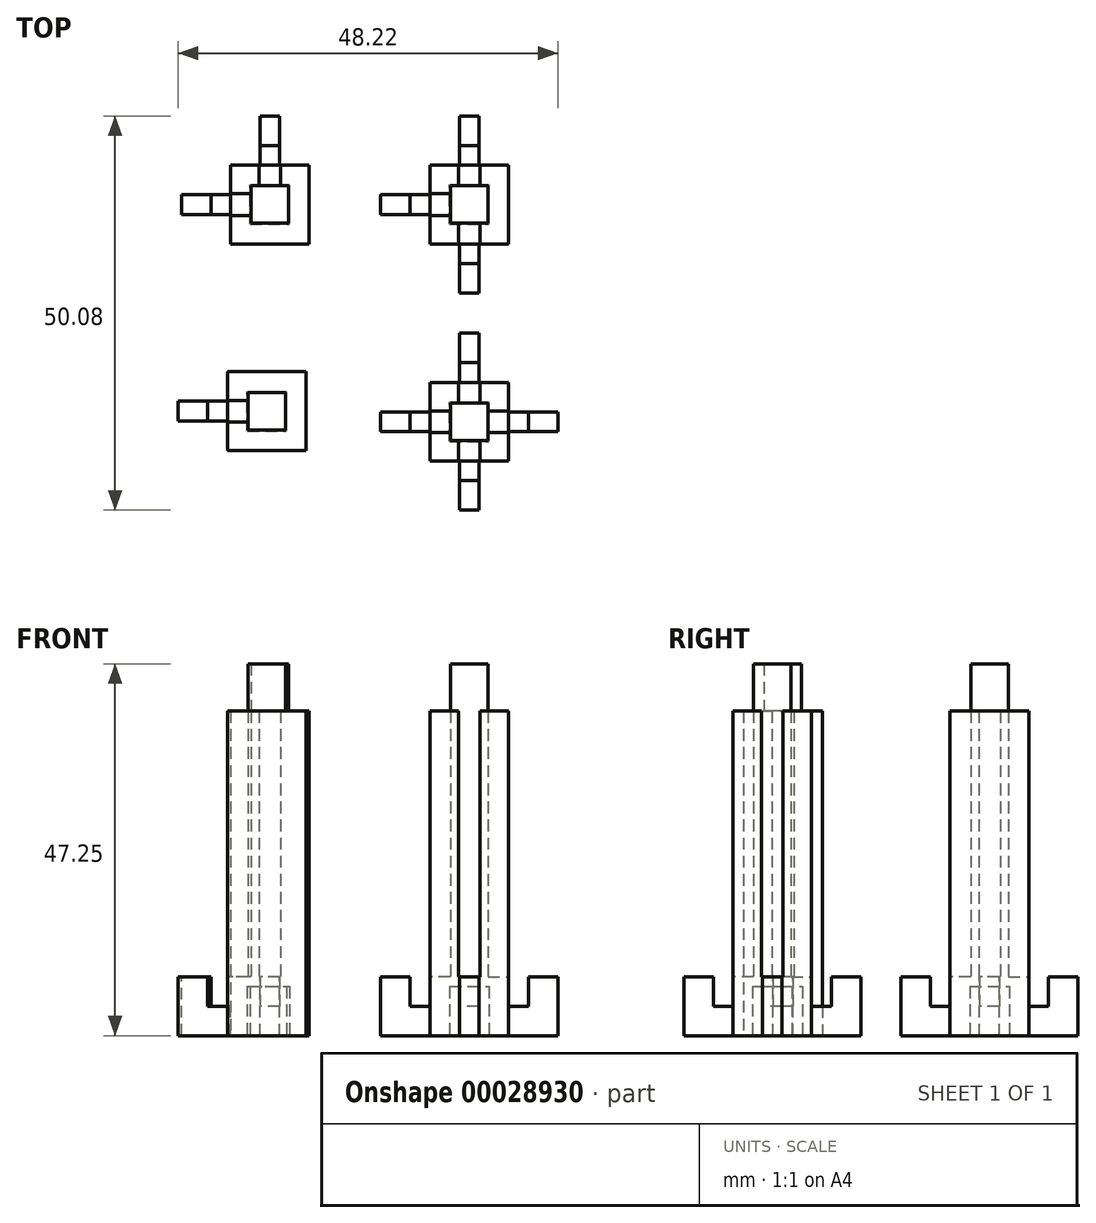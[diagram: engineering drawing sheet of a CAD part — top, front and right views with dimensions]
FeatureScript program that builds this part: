
annotation { "Feature Type Name" : "Feature", "Feature Type Description" : "" }
export const myFeature = defineFeature(function(context is Context, id is Id, definition is map)
    precondition{}
    {
        {
            var Q0;
            Q0=qCreatedBy(makeId("Top.planeOp"),FACE);
            var sketch = newSketch(context, id + "F0", { "sketchPlane" : qUnion([Q0])});
            skLineSegment(sketch, "E0.bottom", {"start": v(0, 0) * mm, "end": v(10, 0) * mm});
            skLineSegment(sketch, "E0.top", {"start": v(0, 10) * mm, "end": v(10, 10) * mm});
            skLineSegment(sketch, "E0.left", {"start": v(0, 0) * mm, "end": v(0, 10) * mm});
            skLineSegment(sketch, "E0.right", {"start": v(10, 0) * mm, "end": v(10, 10) * mm});
            skSolve(sketch);
        }
        {
            var Q0;
            Q0=makeQuery(id+"F0.imprint","IMPRINT",FACE,{"disambiguationData":[TD([[makeQuery(id+"F0.imprint","IMPRINT",EDGE,{"derivedFrom":sQuery(id+"F0.wireOp",EDGE,"E0.bottom")}),1.0]])]});
            extrude(context, id + "F1", {"entities" : qUnion([Q0]), "depth" : 41.25 * mm});
        }
        {
            var Q0;
            Q0=makeQuery(id+"F1.opExtrude","CAP_FACE",FACE,{"disambiguationData":[OSD([sQuery(id+"F0.wireOp",EDGE,"E0.bottom"),sQuery(id+"F0.wireOp",EDGE,"E0.top"),sQuery(id+"F0.wireOp",EDGE,"E0.left"),sQuery(id+"F0.wireOp",EDGE,"E0.right")])],"isStart":false});
            var sketch = newSketch(context, id + "F2", { "sketchPlane" : qUnion([Q0])});
            skLineSegment(sketch, "E1.bottom", {"start": v(2.62, 7.38) * mm, "end": v(7.38, 7.38) * mm});
            skLineSegment(sketch, "E1.top", {"start": v(2.62, 2.62) * mm, "end": v(7.38, 2.62) * mm});
            skLineSegment(sketch, "E1.left", {"start": v(2.62, 7.37) * mm, "end": v(2.62, 2.63) * mm});
            skLineSegment(sketch, "E1.right", {"start": v(7.38, 7.37) * mm, "end": v(7.38, 2.63) * mm});
            skLineSegment(sketch, "E2", {"start": v(5, 10) * mm, "end": v(5, 0) * mm, "construction": true});
            skLineSegment(sketch, "E3", {"start": v(0, 5) * mm, "end": v(10, 5) * mm, "construction": true});
            skSolve(sketch);
        }
        {
            var Q0;
            Q0=makeQuery(id+"F2.imprint","IMPRINT",FACE,{"disambiguationData":[TD([[makeQuery(id+"F2.imprint","IMPRINT",EDGE,{"derivedFrom":sQuery(id+"F2.wireOp",EDGE,"E1.bottom")}),-1.0]])]});
            extrude(context, id + "F3", {"entities" : qUnion([Q0]), "operationType" : NewBodyOperationType.ADD, "depth" : 6 * mm});
        }
        {
            var Q0;
            Q0=makeQuery(id+"F1.opExtrude","CAP_FACE",FACE,{"disambiguationData":[OSD([sQuery(id+"F0.wireOp",EDGE,"E0.bottom"),sQuery(id+"F0.wireOp",EDGE,"E0.top"),sQuery(id+"F0.wireOp",EDGE,"E0.left"),sQuery(id+"F0.wireOp",EDGE,"E0.right")])],"isStart":true});
            var sketch = newSketch(context, id + "F4", { "sketchPlane" : qUnion([Q0])});
            skLineSegment(sketch, "E4.bottom", {"start": v(2.5, -2.5) * mm, "end": v(7.5, -2.5) * mm});
            skLineSegment(sketch, "E4.top", {"start": v(2.5, -7.5) * mm, "end": v(7.5, -7.5) * mm});
            skLineSegment(sketch, "E4.left", {"start": v(2.5, -2.5) * mm, "end": v(2.5, -7.5) * mm});
            skLineSegment(sketch, "E4.right", {"start": v(7.5, -2.5) * mm, "end": v(7.5, -7.5) * mm});
            skLineSegment(sketch, "E5", {"start": v(0, 0) * mm, "end": v(10, -10) * mm, "construction": true});
            skLineSegment(sketch, "E6", {"start": v(10, 0) * mm, "end": v(0, -10) * mm, "construction": true});
            skSolve(sketch);
        }
        {
            var Q0;
            Q0=makeQuery(id+"F4.imprint","IMPRINT",FACE,{"disambiguationData":[TD([[makeQuery(id+"F4.imprint","IMPRINT",EDGE,{"derivedFrom":sQuery(id+"F4.wireOp",EDGE,"E4.bottom")}),-1.0]])]});
            extrude(context, id + "F5", {"entities" : qUnion([Q0]), "operationType" : NewBodyOperationType.REMOVE, "oppositeDirection" : true, "depth" : 6.25 * mm});
        }
        {
            var Q0;
            Q0=makeQuery(id+"F1.opExtrude","SWEPT_FACE",FACE,{"disambiguationData":[OSD([sQuery(id+"F0.wireOp",EDGE,"E0.left")])]});
            var sketch = newSketch(context, id + "F6", { "sketchPlane" : qUnion([Q0])});
            skLineSegment(sketch, "E7.bottom", {"start": v(-6.25, 0) * mm, "end": v(-3.75, 0) * mm});
            skLineSegment(sketch, "E7.top", {"start": v(-6.25, 7.5) * mm, "end": v(-3.75, 7.5) * mm});
            skLineSegment(sketch, "E7.left", {"start": v(-6.25, 0) * mm, "end": v(-6.25, 7.5) * mm});
            skLineSegment(sketch, "E7.right", {"start": v(-3.75, 0) * mm, "end": v(-3.75, 7.5) * mm});
            skLineSegment(sketch, "E8", {"start": v(-5, 0) * mm, "end": v(-5, 41.25) * mm, "construction": true});
            skLineSegment(sketch, "E9.bottom", {"start": v(-6.37, 41.25) * mm, "end": v(-3.63, 41.25) * mm});
            skLineSegment(sketch, "E9.top", {"start": v(-6.37, 7.5) * mm, "end": v(-3.62, 7.5) * mm});
            skLineSegment(sketch, "E9.left", {"start": v(-6.37, 41.25) * mm, "end": v(-6.37, 7.5) * mm});
            skLineSegment(sketch, "E9.right", {"start": v(-3.63, 41.25) * mm, "end": v(-3.62, 7.5) * mm});
            skSolve(sketch);
        }
        {
            var Q0;
            Q0=makeQuery(id+"F6.imprint","IMPRINT",FACE,{"disambiguationData":[TD([[makeQuery(id+"F6.imprint","IMPRINT",EDGE,{"derivedFrom":sQuery(id+"F6.wireOp",EDGE,"E9.bottom")}),1.0]])]});
            extrude(context, id + "F7", {"entities" : qUnion([Q0]), "operationType" : NewBodyOperationType.REMOVE, "oppositeDirection" : true, "depth" : 2.62 * mm});
        }
        {
            var Q0;
            Q0=makeQuery(id+"F6.imprint","IMPRINT",FACE,{"disambiguationData":[TD([[makeQuery(id+"F6.imprint","IMPRINT",EDGE,{"derivedFrom":sQuery(id+"F6.wireOp",EDGE,"E7.bottom")}),-1.0]])]});
            extrude(context, id + "F8", {"entities" : qUnion([Q0]), "operationType" : NewBodyOperationType.ADD, "depth" : (3.75 + 2.5) * mm});
        }
        {
            var Q0;
            Q0=makeQuery(id+"F8.opExtrude","SWEPT_FACE",FACE,{"disambiguationData":[OSD([sQuery(id+"F6.wireOp",EDGE,"E7.right")])]});
            var sketch = newSketch(context, id + "F9", { "sketchPlane" : qUnion([Q0])});
            skLineSegment(sketch, "E10.bottom", {"start": v(0, 7.5) * mm, "end": v(-2.5, 7.5) * mm});
            skLineSegment(sketch, "E10.top", {"start": v(0, 3.75) * mm, "end": v(-2.5, 3.75) * mm});
            skLineSegment(sketch, "E10.left", {"start": v(0, 7.5) * mm, "end": v(0, 3.75) * mm});
            skLineSegment(sketch, "E10.right", {"start": v(-2.5, 7.5) * mm, "end": v(-2.5, 3.75) * mm});
            skSolve(sketch);
        }
        {
            var Q0;
            Q0=makeQuery(id+"F9.imprint","IMPRINT",FACE,{"disambiguationData":[TD([[makeQuery(id+"F9.imprint","IMPRINT",EDGE,{"derivedFrom":sQuery(id+"F9.wireOp",EDGE,"E10.bottom")}),-1.0]])]});
            extrude(context, id + "F10", {"entities" : qUnion([Q0]), "operationType" : NewBodyOperationType.REMOVE, "endBound" : BoundingType.UP_TO_NEXT, "oppositeDirection" : true, "depth" : 25 * mm});
        }
        {
            var Q0;
            Q0=makeQuery(id+"F1.opExtrude","SWEPT_BODY",BODY,{"disambiguationData":[OSD([sQuery(id+"F0.wireOp",EDGE,"E0.bottom"),sQuery(id+"F0.wireOp",EDGE,"E0.top"),sQuery(id+"F0.wireOp",EDGE,"E0.left"),sQuery(id+"F0.wireOp",EDGE,"E0.right")])]});
            transform(context, id + "F11", {"entities" : qUnion([Q0]), "transformType" : TransformType.TRANSLATION_3D, "dx" : 0.4 * mm, "dy" : 26.24 * mm, "dz" : 0 * mm, "makeCopy" : true});
        }
        {
            var Q0;
            Q0=makeQuery(id+"F11.opPattern","COPY",FACE,{"derivedFrom":makeQuery(id+"F1.opExtrude","SWEPT_FACE",FACE,{"disambiguationData":[OSD([sQuery(id+"F0.wireOp",EDGE,"E0.top")])]}),"instanceName":"1"});
            var sketch = newSketch(context, id + "F12", { "sketchPlane" : qUnion([Q0])});
            skLineSegment(sketch, "E11.bottom", {"start": v(-6.65, 0) * mm, "end": v(-4.15, 0) * mm});
            skLineSegment(sketch, "E11.top", {"start": v(-6.65, 7.5) * mm, "end": v(-4.15, 7.5) * mm});
            skLineSegment(sketch, "E11.left", {"start": v(-6.65, 0) * mm, "end": v(-6.65, 7.5) * mm});
            skLineSegment(sketch, "E11.right", {"start": v(-4.15, 0) * mm, "end": v(-4.15, 7.5) * mm});
            skLineSegment(sketch, "E12", {"start": v(-5.4, 0) * mm, "end": v(-5.4, 41.25) * mm, "construction": true});
            skLineSegment(sketch, "E13.bottom", {"start": v(-6.78, 41.25) * mm, "end": v(-4.03, 41.25) * mm});
            skLineSegment(sketch, "E13.top", {"start": v(-6.77, 7.5) * mm, "end": v(-4.02, 7.5) * mm});
            skLineSegment(sketch, "E13.left", {"start": v(-6.78, 41.25) * mm, "end": v(-6.77, 7.5) * mm});
            skLineSegment(sketch, "E13.right", {"start": v(-4.03, 41.25) * mm, "end": v(-4.02, 7.5) * mm});
            skSolve(sketch);
        }
        {
            var Q0;
            Q0=makeQuery(id+"F12.imprint","IMPRINT",FACE,{"disambiguationData":[TD([[makeQuery(id+"F12.imprint","IMPRINT",EDGE,{"derivedFrom":sQuery(id+"F12.wireOp",EDGE,"E13.bottom")}),1.0]])]});
            extrude(context, id + "F13", {"entities" : qUnion([Q0]), "operationType" : NewBodyOperationType.REMOVE, "oppositeDirection" : true, "depth" : 2.62 * mm});
        }
        {
            var Q0;
            Q0=makeQuery(id+"F12.imprint","IMPRINT",FACE,{"disambiguationData":[TD([[makeQuery(id+"F12.imprint","IMPRINT",EDGE,{"derivedFrom":sQuery(id+"F12.wireOp",EDGE,"E11.bottom")}),-1.0]])]});
            extrude(context, id + "F14", {"entities" : qUnion([Q0]), "operationType" : NewBodyOperationType.ADD, "depth" : (3.75 + 2.5) * mm});
        }
        {
            var Q0;
            Q0=makeQuery(id+"F14.opExtrude","SWEPT_FACE",FACE,{"disambiguationData":[OSD([sQuery(id+"F12.wireOp",EDGE,"E11.right")])]});
            var sketch = newSketch(context, id + "F15", { "sketchPlane" : qUnion([Q0])});
            skLineSegment(sketch, "E14.bottom", {"start": v(-36.24, 7.5) * mm, "end": v(-38.74, 7.5) * mm});
            skLineSegment(sketch, "E14.top", {"start": v(-36.24, 3.75) * mm, "end": v(-38.74, 3.75) * mm});
            skLineSegment(sketch, "E14.left", {"start": v(-36.24, 7.5) * mm, "end": v(-36.24, 3.75) * mm});
            skLineSegment(sketch, "E14.right", {"start": v(-38.74, 7.5) * mm, "end": v(-38.74, 3.75) * mm});
            skSolve(sketch);
        }
        {
            var Q0;
            Q0=makeQuery(id+"F15.imprint","IMPRINT",FACE,{"disambiguationData":[TD([[makeQuery(id+"F15.imprint","IMPRINT",EDGE,{"derivedFrom":sQuery(id+"F15.wireOp",EDGE,"E14.bottom")}),-1.0]])]});
            extrude(context, id + "F16", {"entities" : qUnion([Q0]), "operationType" : NewBodyOperationType.REMOVE, "endBound" : BoundingType.UP_TO_NEXT, "oppositeDirection" : true, "depth" : 25 * mm});
        }
        {
            var Q0;
            Q0=makeQuery(id+"F11.opPattern","COPY",BODY,{"derivedFrom":makeQuery(id+"F1.opExtrude","SWEPT_BODY",BODY,{"disambiguationData":[OSD([sQuery(id+"F0.wireOp",EDGE,"E0.bottom"),sQuery(id+"F0.wireOp",EDGE,"E0.top"),sQuery(id+"F0.wireOp",EDGE,"E0.left"),sQuery(id+"F0.wireOp",EDGE,"E0.right")])]}),"instanceName":"1"});
            transform(context, id + "F17", {"entities" : qUnion([Q0]), "transformType" : TransformType.TRANSLATION_3D, "dx" : 25.32 * mm, "dy" : 0 * mm, "dz" : 0 * mm, "makeCopy" : true});
        }
        {
            var Q0;
            Q0=makeQuery(id+"F17.opPattern","COPY",FACE,{"derivedFrom":makeQuery(id+"F11.opPattern","COPY",FACE,{"derivedFrom":makeQuery(id+"F1.opExtrude","SWEPT_FACE",FACE,{"disambiguationData":[OSD([sQuery(id+"F0.wireOp",EDGE,"E0.bottom")])]}),"instanceName":"1"}),"instanceName":"1"});
            var sketch = newSketch(context, id + "F18", { "sketchPlane" : qUnion([Q0])});
            skLineSegment(sketch, "E15.bottom", {"start": v(29.47, 0) * mm, "end": v(31.97, 0) * mm});
            skLineSegment(sketch, "E15.top", {"start": v(29.47, 7.5) * mm, "end": v(31.97, 7.5) * mm});
            skLineSegment(sketch, "E15.left", {"start": v(29.47, 0) * mm, "end": v(29.47, 7.5) * mm});
            skLineSegment(sketch, "E15.right", {"start": v(31.97, 0) * mm, "end": v(31.97, 7.5) * mm});
            skLineSegment(sketch, "E16", {"start": v(30.72, 0) * mm, "end": v(30.72, 41.25) * mm, "construction": true});
            skLineSegment(sketch, "E17.bottom", {"start": v(29.34, 41.25) * mm, "end": v(32.1, 41.25) * mm});
            skLineSegment(sketch, "E17.top", {"start": v(29.34, 7.5) * mm, "end": v(32.1, 7.5) * mm});
            skLineSegment(sketch, "E17.left", {"start": v(29.34, 41.25) * mm, "end": v(29.34, 7.5) * mm});
            skLineSegment(sketch, "E17.right", {"start": v(32.1, 41.25) * mm, "end": v(32.1, 7.5) * mm});
            skSolve(sketch);
        }
        {
            var Q0;
            Q0=makeQuery(id+"F18.imprint","IMPRINT",FACE,{"disambiguationData":[TD([[makeQuery(id+"F18.imprint","IMPRINT",EDGE,{"derivedFrom":sQuery(id+"F18.wireOp",EDGE,"E17.bottom")}),-1.0]])]});
            extrude(context, id + "F19", {"entities" : qUnion([Q0]), "operationType" : NewBodyOperationType.REMOVE, "oppositeDirection" : true, "depth" : 2.62 * mm});
        }
        {
            var Q0;
            Q0=makeQuery(id+"F18.imprint","IMPRINT",FACE,{"disambiguationData":[TD([[makeQuery(id+"F18.imprint","IMPRINT",EDGE,{"derivedFrom":sQuery(id+"F18.wireOp",EDGE,"E15.bottom")}),1.0]])]});
            extrude(context, id + "F20", {"entities" : qUnion([Q0]), "operationType" : NewBodyOperationType.ADD, "depth" : (3.75 + 2.5) * mm});
        }
        {
            var Q0;
            Q0=makeQuery(id+"F20.opExtrude","SWEPT_FACE",FACE,{"disambiguationData":[OSD([sQuery(id+"F18.wireOp",EDGE,"E15.right")])]});
            var sketch = newSketch(context, id + "F21", { "sketchPlane" : qUnion([Q0])});
            skLineSegment(sketch, "E18.bottom", {"start": v(26.24, 7.5) * mm, "end": v(23.74, 7.5) * mm});
            skLineSegment(sketch, "E18.top", {"start": v(26.24, 3.75) * mm, "end": v(23.74, 3.75) * mm});
            skLineSegment(sketch, "E18.left", {"start": v(26.24, 7.5) * mm, "end": v(26.24, 3.75) * mm});
            skLineSegment(sketch, "E18.right", {"start": v(23.74, 7.5) * mm, "end": v(23.74, 3.75) * mm});
            skSolve(sketch);
        }
        {
            var Q0;
            Q0=makeQuery(id+"F21.imprint","IMPRINT",FACE,{"disambiguationData":[TD([[makeQuery(id+"F21.imprint","IMPRINT",EDGE,{"derivedFrom":sQuery(id+"F21.wireOp",EDGE,"E18.bottom")}),-1.0]])]});
            extrude(context, id + "F22", {"entities" : qUnion([Q0]), "operationType" : NewBodyOperationType.REMOVE, "endBound" : BoundingType.UP_TO_NEXT, "oppositeDirection" : true, "depth" : 25 * mm});
        }
        {
            var Q0;
            Q0=makeQuery(id+"F17.opPattern","COPY",BODY,{"derivedFrom":makeQuery(id+"F11.opPattern","COPY",BODY,{"derivedFrom":makeQuery(id+"F1.opExtrude","SWEPT_BODY",BODY,{"disambiguationData":[OSD([sQuery(id+"F0.wireOp",EDGE,"E0.bottom"),sQuery(id+"F0.wireOp",EDGE,"E0.top"),sQuery(id+"F0.wireOp",EDGE,"E0.left"),sQuery(id+"F0.wireOp",EDGE,"E0.right")])]}),"instanceName":"1"}),"instanceName":"1"});
            transform(context, id + "F23", {"entities" : qUnion([Q0]), "transformType" : TransformType.TRANSLATION_3D, "dx" : 0 * mm, "dy" : -27.59 * mm, "dz" : 0 * mm, "makeCopy" : true});
        }
        {
            var Q0;
            Q0=makeQuery(id+"F23.opPattern","COPY",FACE,{"derivedFrom":makeQuery(id+"F17.opPattern","COPY",FACE,{"derivedFrom":makeQuery(id+"F11.opPattern","COPY",FACE,{"derivedFrom":makeQuery(id+"F1.opExtrude","SWEPT_FACE",FACE,{"disambiguationData":[OSD([sQuery(id+"F0.wireOp",EDGE,"E0.right")])]}),"instanceName":"1"}),"instanceName":"1"}),"instanceName":"1"});
            var sketch = newSketch(context, id + "F24", { "sketchPlane" : qUnion([Q0])});
            skLineSegment(sketch, "E19.bottom", {"start": v(2.4, 0) * mm, "end": v(4.9, 0) * mm});
            skLineSegment(sketch, "E19.top", {"start": v(2.4, 7.5) * mm, "end": v(4.9, 7.5) * mm});
            skLineSegment(sketch, "E19.left", {"start": v(2.4, 0) * mm, "end": v(2.4, 7.5) * mm});
            skLineSegment(sketch, "E19.right", {"start": v(4.9, 0) * mm, "end": v(4.9, 7.5) * mm});
            skLineSegment(sketch, "E20", {"start": v(3.66, 0) * mm, "end": v(3.66, 41.25) * mm, "construction": true});
            skLineSegment(sketch, "E21.bottom", {"start": v(2.28, 41.25) * mm, "end": v(5.03, 41.25) * mm});
            skLineSegment(sketch, "E21.top", {"start": v(2.28, 7.5) * mm, "end": v(5.03, 7.5) * mm});
            skLineSegment(sketch, "E21.left", {"start": v(2.28, 41.25) * mm, "end": v(2.28, 7.5) * mm});
            skLineSegment(sketch, "E21.right", {"start": v(5.03, 41.25) * mm, "end": v(5.03, 7.5) * mm});
            skSolve(sketch);
        }
        {
            var Q0;
            Q0=makeQuery(id+"F24.imprint","IMPRINT",FACE,{"disambiguationData":[TD([[makeQuery(id+"F24.imprint","IMPRINT",EDGE,{"derivedFrom":sQuery(id+"F24.wireOp",EDGE,"E21.bottom")}),-1.0]])]});
            extrude(context, id + "F25", {"entities" : qUnion([Q0]), "operationType" : NewBodyOperationType.REMOVE, "oppositeDirection" : true, "depth" : 2.62 * mm});
        }
        {
            var Q0;
            Q0=makeQuery(id+"F24.imprint","IMPRINT",FACE,{"disambiguationData":[TD([[makeQuery(id+"F24.imprint","IMPRINT",EDGE,{"derivedFrom":sQuery(id+"F24.wireOp",EDGE,"E19.bottom")}),1.0]])]});
            extrude(context, id + "F26", {"entities" : qUnion([Q0]), "operationType" : NewBodyOperationType.ADD, "depth" : (3.75 + 2.5) * mm});
        }
        {
            var Q0;
            Q0=makeQuery(id+"F26.opExtrude","SWEPT_FACE",FACE,{"disambiguationData":[OSD([sQuery(id+"F24.wireOp",EDGE,"E19.right")])]});
            var sketch = newSketch(context, id + "F27", { "sketchPlane" : qUnion([Q0])});
            skLineSegment(sketch, "E22.bottom", {"start": v(-35.72, 7.5) * mm, "end": v(-38.22, 7.5) * mm});
            skLineSegment(sketch, "E22.top", {"start": v(-35.72, 3.75) * mm, "end": v(-38.22, 3.75) * mm});
            skLineSegment(sketch, "E22.left", {"start": v(-35.72, 7.5) * mm, "end": v(-35.72, 3.75) * mm});
            skLineSegment(sketch, "E22.right", {"start": v(-38.22, 7.5) * mm, "end": v(-38.22, 3.75) * mm});
            skSolve(sketch);
        }
        {
            var Q0;
            Q0=makeQuery(id+"F27.imprint","IMPRINT",FACE,{"disambiguationData":[TD([[makeQuery(id+"F27.imprint","IMPRINT",EDGE,{"derivedFrom":sQuery(id+"F27.wireOp",EDGE,"E22.bottom")}),-1.0]])]});
            extrude(context, id + "F28", {"entities" : qUnion([Q0]), "operationType" : NewBodyOperationType.REMOVE, "endBound" : BoundingType.UP_TO_NEXT, "oppositeDirection" : true, "depth" : 25 * mm});
        }
    });
